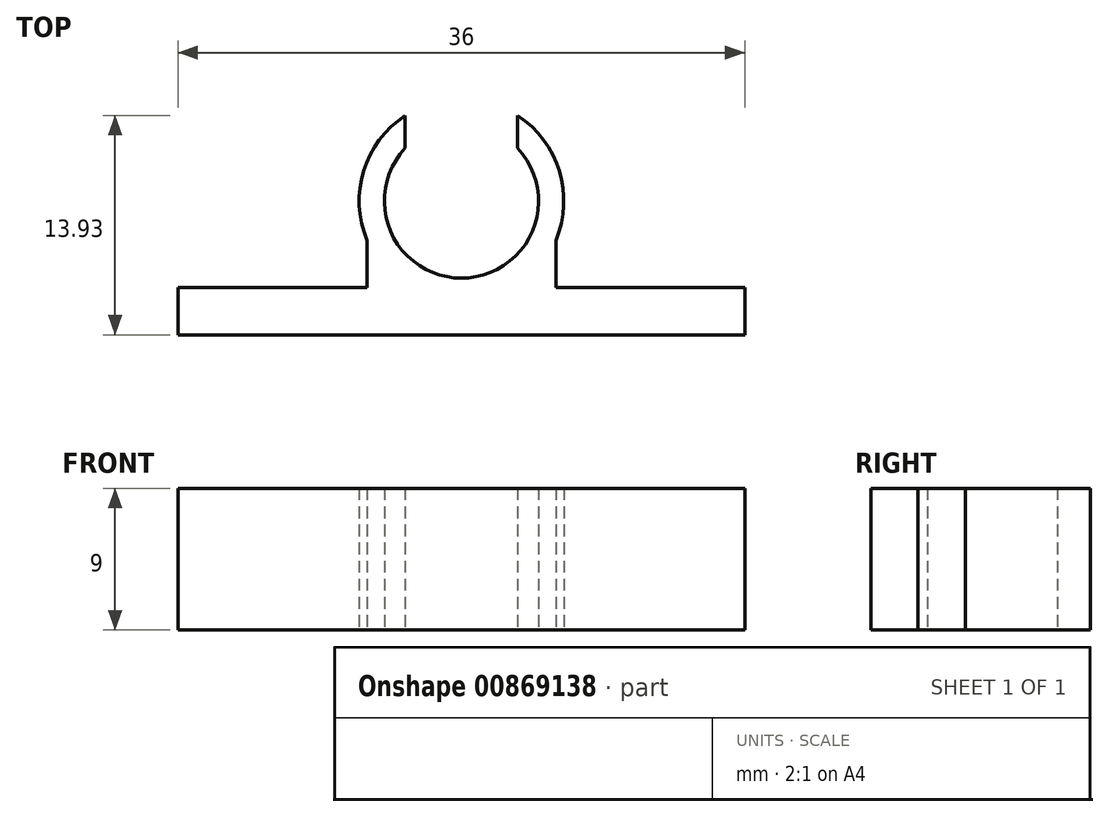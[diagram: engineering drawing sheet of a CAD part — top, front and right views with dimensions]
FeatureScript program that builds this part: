
annotation { "Feature Type Name" : "Feature", "Feature Type Description" : "" }
export const myFeature = defineFeature(function(context is Context, id is Id, definition is map)
    precondition{}
    {
        {
            var Q0;
            Q0=qCreatedBy(makeId("Top.planeOp"),FACE);
            var sketch = newSketch(context, id + "F0", { "sketchPlane" : qUnion([Q0])});
            skArc(sketch, "E0", {"start": v(-3.57, 5.43) * mm, "mid": v(-6.22, 1.9) * mm, "end": v(-6, -2.5) * mm});
            skArc(sketch, "E1", {"start": v(-3.57, 3.35) * mm, "mid": v(0, -4.9) * mm, "end": v(3.57, 3.35) * mm});
            skLineSegment(sketch, "E2.left", {"start": v(6, -5.5) * mm, "end": v(6, -2.5) * mm});
            skLineSegment(sketch, "E2.right", {"start": v(-6, -5.5) * mm, "end": v(-6, -2.5) * mm});
            skPoint(sketch, "E2.middle", {"position": v(0, -6.5) * mm});
            skLineSegment(sketch, "E3", {"start": v(3.57, 3.35) * mm, "end": v(3.57, 5.43) * mm});
            skLineSegment(sketch, "E4", {"start": v(-3.57, 3.35) * mm, "end": v(-3.57, 5.43) * mm});
            skArc(sketch, "E5.trimOffspring", {"start": v(6, -2.5) * mm, "mid": v(6.22, 1.9) * mm, "end": v(3.57, 5.43) * mm});
            skPoint(sketch, "E6.orphan", {"position": v(6, -7.5) * mm});
            skPoint(sketch, "E7.orphan", {"position": v(-6, -7.5) * mm});
            skLineSegment(sketch, "E8", {"start": v(-6, -5.5) * mm, "end": v(-18, -5.5) * mm});
            skLineSegment(sketch, "E9", {"start": v(-18, -5.5) * mm, "end": v(-18, -8.5) * mm});
            skLineSegment(sketch, "E10", {"start": v(-18, -8.5) * mm, "end": v(18, -8.5) * mm});
            skLineSegment(sketch, "E11", {"start": v(18, -8.5) * mm, "end": v(18, -5.5) * mm});
            skLineSegment(sketch, "E12", {"start": v(18, -5.5) * mm, "end": v(6, -5.5) * mm});
            skSolve(sketch);
        }
        {
            var Q0;
            Q0=makeQuery(id+"F0.imprint","IMPRINT",FACE,{"disambiguationData":[TD([[makeQuery(id+"F0.imprint","IMPRINT",EDGE,{"derivedFrom":sQuery(id+"F0.wireOp",EDGE,"E0")}),1.0]])]});
            extrude(context, id + "F1", {"entities" : qUnion([Q0]), "depth" : 9 * mm, "offsetDistance" : 25 * mm});
        }
    });
